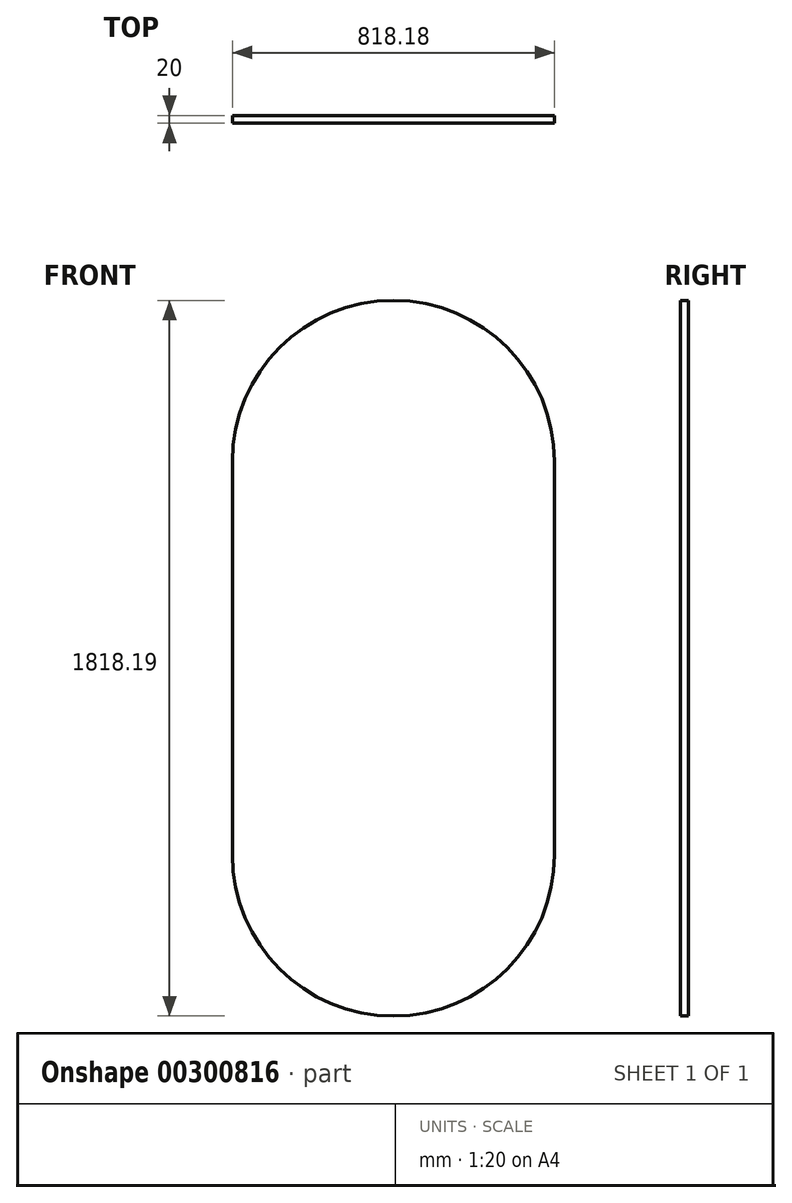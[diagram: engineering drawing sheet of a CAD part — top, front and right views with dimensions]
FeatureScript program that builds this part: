
annotation { "Feature Type Name" : "Feature", "Feature Type Description" : "" }
export const myFeature = defineFeature(function(context is Context, id is Id, definition is map)
    precondition{}
    {
        {
            var Q0;
            Q0=qCreatedBy(makeId("Front.planeOp"),FACE);
            var sketch = newSketch(context, id + "F0", { "sketchPlane" : qUnion([Q0])});
            skLineSegment(sketch, "E0.left", {"start": v(0, -699.13) * mm, "end": v(0, 300.87) * mm});
            skLineSegment(sketch, "E0.right", {"start": v(818.18, -699.13) * mm, "end": v(818.18, 300.87) * mm});
            skArc(sketch, "E1", {"start": v(818.18, -699.13) * mm, "mid": v(409.1, -1108.23) * mm, "end": v(0, -699.13) * mm});
            skArc(sketch, "E2", {"start": v(0, 300.87) * mm, "mid": v(409.1, 709.96) * mm, "end": v(818.18, 300.87) * mm});
            skSolve(sketch);
        }
        {
            var Q0;
            Q0 = qSketchRegion(id + "F0", true);
            extrude(context, id + "F1", {"entities" : qUnion([Q0]), "depth" : 20 * mm});
        }
    });
